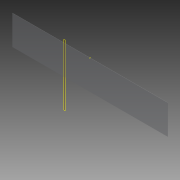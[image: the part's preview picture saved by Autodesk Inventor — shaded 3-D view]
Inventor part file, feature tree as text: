
AUTODESK INVENTOR PART (.ipt)
format: ipt  version: 2013 (Build 170138000, 138)  size: 86,528 bytes
history: native  units: in
note: dims shown in document units (in); Inventor stores cm internally (conversion verified against a paired STEP export)
features: reference x5, plane x2, extrude x1, sketch x1
ambient origin geometry x8: Origin, YZ Plane, XZ Plane, XY Plane, X Axis, Y Axis, Z Axis, Center Point
bodies: Solid1 (feature_tree)
feature tree (9):
  plane  "Work Plane1"
  extrude  "Extrusion1"  [1 undecoded]
  plane  "Work Plane2"
  sketch  "Sketch1"  dims[d0=0.25in d1=0.0in]
  reference  "Reference1"
  reference  "Reference2"
  reference  "Reference3"
  reference  "Reference4"
  reference  "Reference5"
note: 1 required parameter value undecoded (feature->parameter linkage not recoverable at this tier; creation-order binding heuristic only, values carry confidence <= 0.55)
